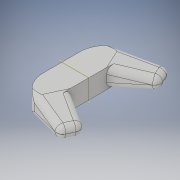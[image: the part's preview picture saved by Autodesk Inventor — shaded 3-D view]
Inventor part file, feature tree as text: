
AUTODESK INVENTOR PART (.ipt)
format: ipt  version: 2018 (Build 220112000, 112)  size: 175,616 bytes
history: native  units: in
note: dims shown in document units (in); Inventor stores cm internally (conversion verified against a paired STEP export)
features: sketch x3, extrude x2, revolve x1, plane x1, mirror x1, fillet x1
ambient origin geometry x8: Origin, YZ Plane, XZ Plane, XY Plane, X Axis, Y Axis, Z Axis, Center Point
bodies: Solid1 (feature_tree)
feature tree (9):
  extrude  "Extrusion1"  Depth=3.7402in
  revolve  "Revolution1"  [1 undecoded]
  extrude  "Extrusion2"  [1 undecoded]
  plane  "Work Plane1"
  mirror  "Mirror1"
  fillet  "Fillet1"  Radius=0.63in
  sketch  "Sketch1"  dims[d0=2.7559in d1=3.7402in]
  sketch  "Sketch2"  dims[d2=1.9685in d3=0.0in d4=0.4466in]
  sketch  "Sketch3"  dims[d5=3.937in d6=-0.0412in d7=-1.8701in d8=0.63in]
note: 2 required parameter values undecoded (feature->parameter linkage not recoverable at this tier; creation-order binding heuristic only, values carry confidence <= 0.55)